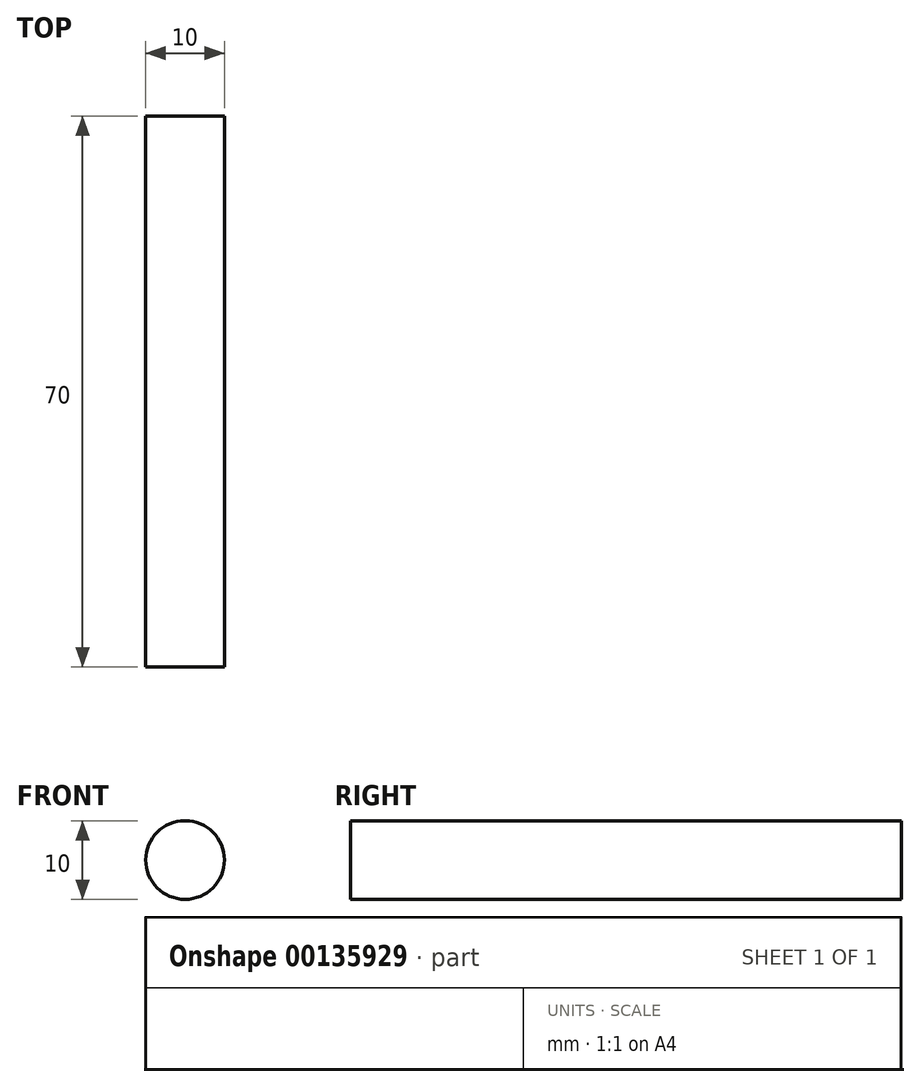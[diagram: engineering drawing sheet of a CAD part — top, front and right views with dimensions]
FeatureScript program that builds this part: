
annotation { "Feature Type Name" : "Feature", "Feature Type Description" : "" }
export const myFeature = defineFeature(function(context is Context, id is Id, definition is map)
    precondition{}
    {
        {
            var Q0;
            Q0=qCreatedBy(makeId("Front.planeOp"),FACE);
            var sketch = newSketch(context, id + "F0", { "sketchPlane" : qUnion([Q0])});
            skCircle(sketch, "E0", {"center": v(0, 0) * mm, "radius": 5 * mm});
            skLineSegment(sketch, "E1", {"start": v(0, 0) * mm, "end": v(5, 0) * mm});
            skSolve(sketch);
        }
        {
            var Q0;
            Q0=qSketchRegion(id+"F0",true);
            extrude(context, id + "F1", {"entities" : qUnion([Q0]), "depth" : 35 * mm, "hasSecondDirection" : true, "secondDirectionOppositeDirection" : true, "secondDirectionDepth" : 35 * mm});
        }
    });
